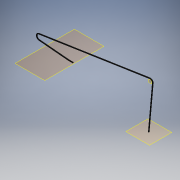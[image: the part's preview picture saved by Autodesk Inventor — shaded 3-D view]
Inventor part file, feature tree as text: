
AUTODESK INVENTOR PART (.ipt)
format: ipt  version: 2017 (Build 210142000, 142)  size: 181,760 bytes
history: native  units: mm
features: other x4, plane x3, sketch x3, reference x2, sweep x1
ambient origin geometry x8: Origin, YZ Plane, XZ Plane, XY Plane, X Axis, Y Axis, Z Axis, Center Point
bodies: Body1 (feature_tree)
feature tree (13):
  plane  "Work Plane3"
  plane  "Work Plane5"
  sketch  "Sketch4"
  sketch  "3D Sketch1"
  plane  "Work Plane2"
  sweep  "Sweep2"
  sketch  "Sketch2"  dims[d0=8.0mm d3=0.0mm d4=0.0mm]
  reference  "Reference1"
  reference  "Reference3"
  other  "<userpath>\OneDrive\Inventor\VolledigGeassembleerdv001.iam"
  other  "VolledigGeassembleerdv001.iam"
  other  "winch:1"
  other  "emmerhouder:1"
